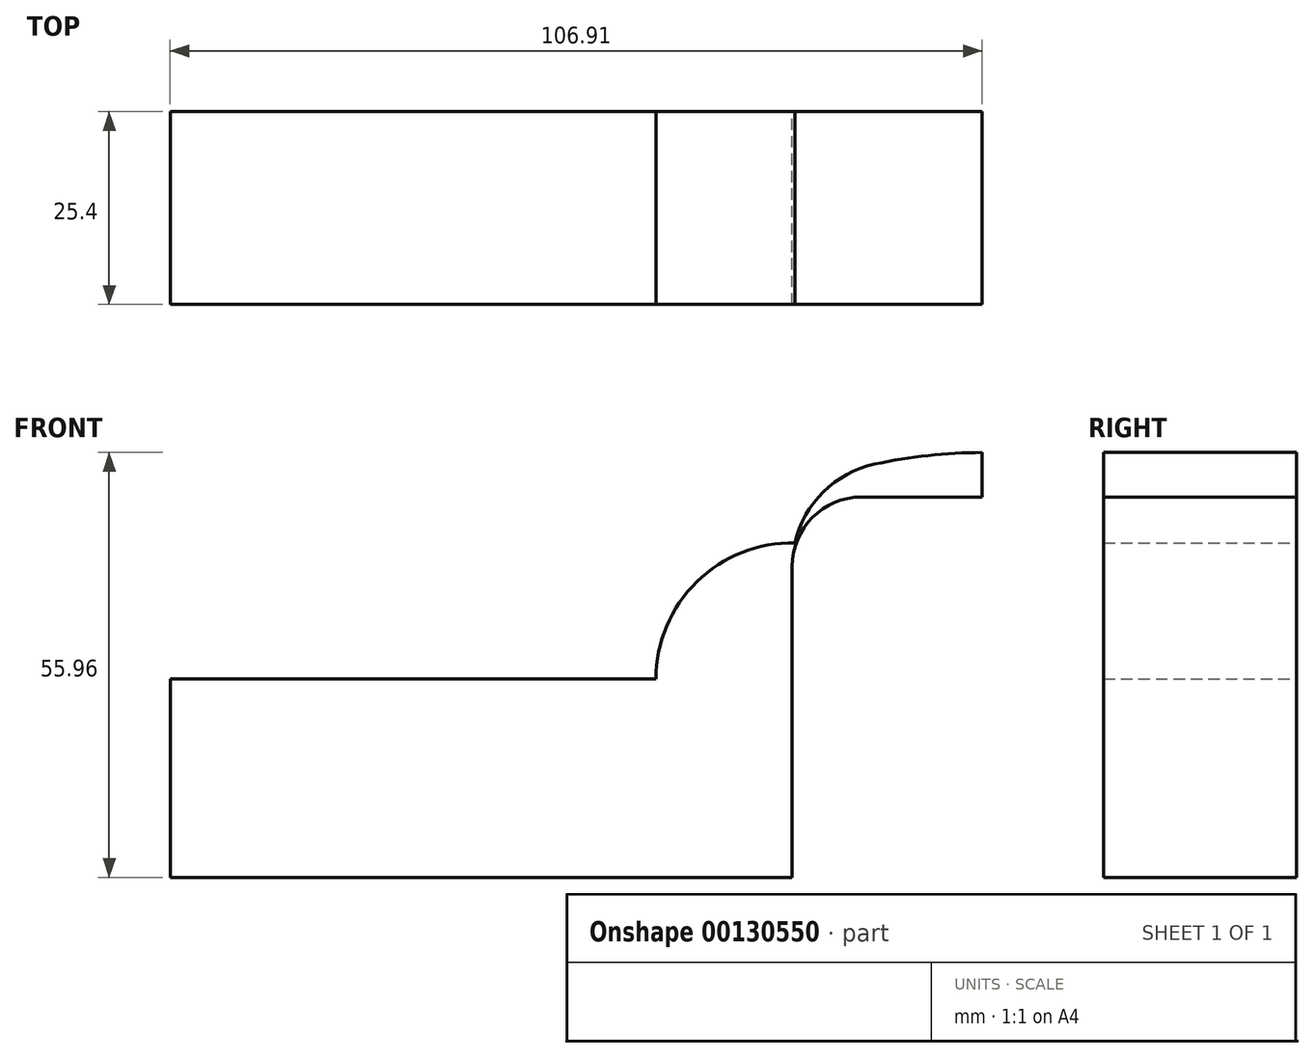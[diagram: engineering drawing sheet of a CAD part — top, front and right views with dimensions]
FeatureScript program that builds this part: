
annotation { "Feature Type Name" : "Feature", "Feature Type Description" : "" }
export const myFeature = defineFeature(function(context is Context, id is Id, definition is map)
    precondition{}
    {
        {
            var Q0;
            Q0=qCreatedBy(makeId("Front.planeOp"),FACE);
            var sketch = newSketch(context, id + "F0", { "sketchPlane" : qUnion([Q0])});
            skLineSegment(sketch, "E0.bottom", {"start": v(-69.45, 43.89) * mm, "end": v(12.45, 43.89) * mm});
            skLineSegment(sketch, "E0.top", {"start": v(-69.45, 17.75) * mm, "end": v(12.45, 17.75) * mm});
            skLineSegment(sketch, "E0.left", {"start": v(-69.45, 43.89) * mm, "end": v(-69.45, 17.75) * mm});
            skLineSegment(sketch, "E0.right", {"start": v(12.45, 43.89) * mm, "end": v(12.45, 17.75) * mm});
            skLineSegment(sketch, "E1.bottom", {"start": v(37.46, 82.76) * mm, "end": v(67.09, 82.76) * mm});
            skLineSegment(sketch, "E1.top", {"start": v(37.46, 57.36) * mm, "end": v(67.09, 57.36) * mm});
            skLineSegment(sketch, "E1.left", {"start": v(37.46, 82.76) * mm, "end": v(37.46, 57.36) * mm});
            skLineSegment(sketch, "E1.right", {"start": v(67.09, 82.76) * mm, "end": v(67.09, 57.36) * mm});
            skLineSegment(sketch, "E2", {"start": v(12.45, 43.89) * mm, "end": v(12.45, 58.7) * mm});
            skArc(sketch, "E3", {"start": v(12.45, 58.7) * mm, "mid": v(15.13, 65.17) * mm, "end": v(21.6, 67.85) * mm});
            skLineSegment(sketch, "E4", {"start": v(21.6, 67.85) * mm, "end": v(51.66, 67.85) * mm});
            skArc(sketch, "E5", {"start": v(12.45, 58.7) * mm, "mid": v(15.51, 67.36) * mm, "end": v(23.33, 72.18) * mm});
            skArc(sketch, "E6", {"start": v(23.33, 72.18) * mm, "mid": v(37.67, 73.71) * mm, "end": v(52.01, 72.18) * mm});
            skArc(sketch, "E7", {"start": v(13, 61.81) * mm, "mid": v(-1.2, 55.5) * mm, "end": v(-5.15, 40.47) * mm});
            skSolve(sketch);
        }
        {
            var Q0;
            Q0=makeQuery(id+"F0.imprint","IMPRINT",FACE,{"disambiguationData":[TD([[makeQuery(id+"F0.imprint","IMPRINT",EDGE,{"derivedFrom":sQuery(id+"F0.wireOp",EDGE,"E0.top")}),1.0]])]});
            var Q1;
            {var subQ0=sQuery(id+"F0.wireOp",EDGE,"E2");Q1=makeQuery(id+"F0.imprint","IMPRINT",FACE,{"disambiguationData":[TD([[makeQuery(id+"F0.imprint","IMPRINT",EDGE,{"derivedFrom":subQ0}),1.0]])]});}
            var Q2;
            {var subQ0=sQuery(id+"F0.wireOp",EDGE,"E6");var subQ8=sQuery(id+"F0.wireOp",EDGE,"E1.left");var subQ11=makeQuery(id+"F0.imprint","INTERSECT",VERTEX,{"derivedFrom":[subQ8,subQ0]});Q2=makeQuery(id+"F0.imprint","IMPRINT",FACE,{"disambiguationData":[TD([[makeQuery(id+"F0.imprint","IMPRINT",EDGE,{"disambiguationData":[TD([[subQ11,-1.0]])],"derivedFrom":subQ8}),-1.0]])]});}
            var Q3;
            {var subQ1=sQuery(id+"F0.wireOp",EDGE,"E3");var subQ3=sQuery(id+"F0.wireOp",EDGE,"E7");var subQ4=makeQuery(id+"F0.imprint","INTERSECT",VERTEX,{"derivedFrom":[subQ1,subQ3]});Q3=makeQuery(id+"F0.imprint","IMPRINT",FACE,{"disambiguationData":[TD([[makeQuery(id+"F0.imprint","IMPRINT",EDGE,{"disambiguationData":[TD([[subQ4,-1.0]])],"derivedFrom":subQ3}),1.0]])]});}
            extrude(context, id + "F1", {"entities" : qUnion([Q0, Q1, Q2, Q3]), "depth" : 25.4 * mm});
        }
    });
